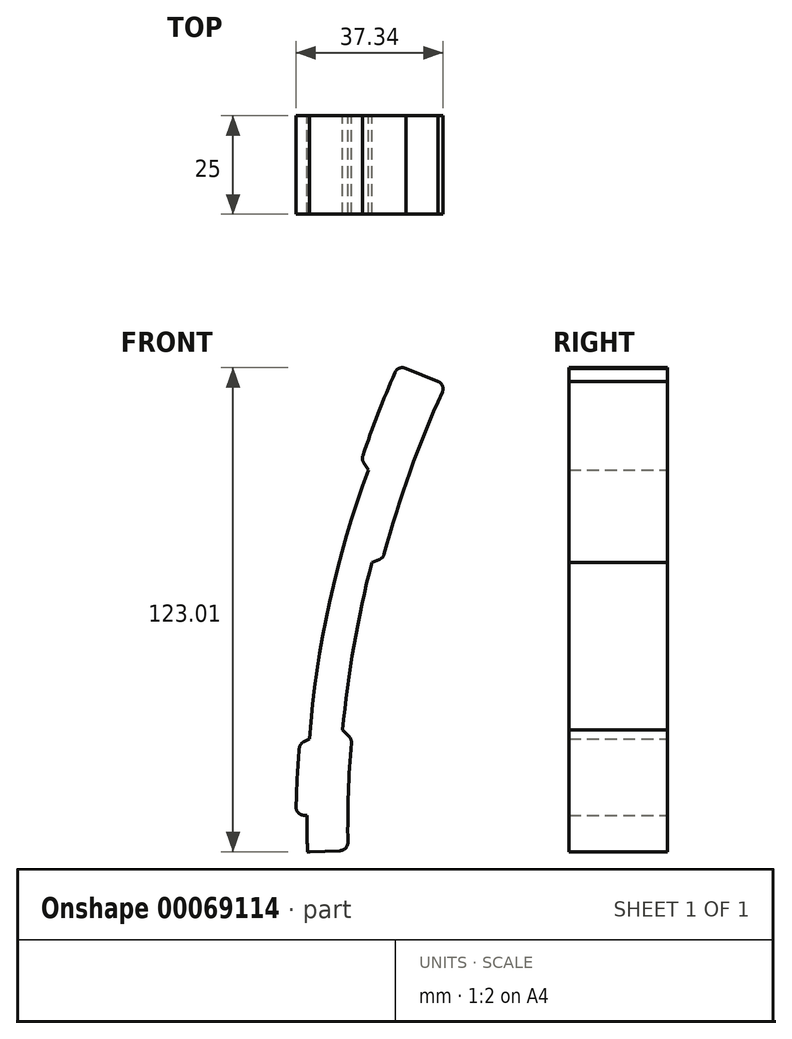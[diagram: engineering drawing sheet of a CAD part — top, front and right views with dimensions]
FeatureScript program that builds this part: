
annotation { "Feature Type Name" : "Feature", "Feature Type Description" : "" }
export const myFeature = defineFeature(function(context is Context, id is Id, definition is map)
    precondition{}
    {
        {
            var Q0;
            Q0=qCreatedBy(makeId("Front.planeOp"),FACE);
            var sketch = newSketch(context, id + "F0", { "sketchPlane" : qUnion([Q0])});
            skArc(sketch, "E0", {"start": v(-249.8, -10) * mm, "mid": v(-249.94, -5.35) * mm, "end": v(-250, -0.7) * mm});
            skArc(sketch, "E1", {"start": v(-250, -10) * mm, "mid": v(-249.6, -10) * mm, "end": v(-249.2, -9.97) * mm});
            skLineSegment(sketch, "E2", {"start": v(-250, -10) * mm, "end": v(-249.2, -9.97) * mm});
            skLineSegment(sketch, "E3", {"start": v(-249.2, -9.97) * mm, "end": v(-241.5, -9.71) * mm});
            skArc(sketch, "E4.trimOffspring", {"start": v(-249.3, 18.65) * mm, "mid": v(-244.24, 53.37) * mm, "end": v(-234.36, 87.04) * mm});
            skArc(sketch, "E5.0", {"start": v(-239.57, -7.69) * mm, "mid": v(-239.42, 5.02) * mm, "end": v(-238.68, 17.71) * mm});
            skArc(sketch, "E6.trimOffspring", {"start": v(-230.32, 65.64) * mm, "mid": v(-223.78, 86.53) * mm, "end": v(-215.57, 106.83) * mm});
            skPoint(sketch, "E7.orphan", {"position": v(-239.02, 13.06) * mm});
            skLineSegment(sketch, "E8", {"start": v(-249.13, 20.78) * mm, "end": v(-249.1, 20.8) * mm});
            skPoint(sketch, "E9.orphan", {"position": v(-248.95, 22.84) * mm});
            skPoint(sketch, "E10.orphan", {"position": v(-250, 1) * mm});
            skArc(sketch, "E11.0", {"start": v(-252.73, 1.35) * mm, "mid": v(-252.42, 8.82) * mm, "end": v(-251.92, 16.27) * mm});
            skArc(sketch, "E12.0", {"start": v(-235.77, 90.65) * mm, "mid": v(-231.9, 101.3) * mm, "end": v(-227.6, 111.8) * mm});
            skArc(sketch, "E13.0", {"start": v(-240.9, 20.93) * mm, "mid": v(-238.03, 42.38) * mm, "end": v(-233.46, 63.54) * mm});
            skLineSegment(sketch, "E14", {"start": v(-233.46, 63.54) * mm, "end": v(-231.53, 64.3) * mm});
            skLineSegment(sketch, "E15", {"start": v(-240.9, 20.93) * mm, "end": v(-239.26, 19.3) * mm});
            skLineSegment(sketch, "E16", {"start": v(-250.81, 17.9) * mm, "end": v(-249.08, 18.76) * mm});
            skPoint(sketch, "E17.visualSharp", {"position": v(-251.83, 17.4) * mm});
            skArc(sketch, "E17.filletArc", {"start": v(-250.81, 17.9) * mm, "mid": v(-251.58, 17.23) * mm, "end": v(-251.92, 16.27) * mm});
            skPoint(sketch, "E18.visualSharp", {"position": v(-252.84, -5.16) * mm});
            skPoint(sketch, "E19.visualSharp", {"position": v(-238.6, 18.64) * mm});
            skArc(sketch, "E19.filletArc", {"start": v(-238.68, 17.71) * mm, "mid": v(-238.8, 18.57) * mm, "end": v(-239.26, 19.3) * mm});
            skPoint(sketch, "E20.visualSharp", {"position": v(-230.58, 64.67) * mm});
            skArc(sketch, "E20.filletArc", {"start": v(-231.53, 64.3) * mm, "mid": v(-230.77, 64.83) * mm, "end": v(-230.32, 65.64) * mm});
            skLineSegment(sketch, "E21", {"start": v(-235.56, 88.94) * mm, "end": v(-234.24, 86.84) * mm});
            skPoint(sketch, "E22.end.orphan", {"position": v(-235.31, 84.43) * mm});
            skPoint(sketch, "E23.visualSharp", {"position": v(-236.07, 89.74) * mm});
            skArc(sketch, "E23.filletArc", {"start": v(-235.77, 90.65) * mm, "mid": v(-235.86, 89.77) * mm, "end": v(-235.56, 88.94) * mm});
            skPoint(sketch, "E24.visualSharp", {"position": v(-226.69, 113.86) * mm});
            skArc(sketch, "E24.filletArc", {"start": v(-224.75, 112.73) * mm, "mid": v(-226.38, 112.9) * mm, "end": v(-227.6, 111.8) * mm});
            skPoint(sketch, "E25.visualSharp", {"position": v(-252.82, -3.11) * mm});
            skLineSegment(sketch, "E26", {"start": v(-250.73, -0.7) * mm, "end": v(-250, -0.7) * mm});
            skArc(sketch, "E27.trimOffspring", {"start": v(-250, 0) * mm, "mid": v(-250, 0) * mm, "end": v(-250, 0) * mm});
            skPoint(sketch, "E28.visualSharp", {"position": v(-252.78, -0.7) * mm});
            skArc(sketch, "E28.filletArc", {"start": v(-252.73, 1.35) * mm, "mid": v(-252.16, -0.1) * mm, "end": v(-250.73, -0.7) * mm});
            skPoint(sketch, "E29.visualSharp", {"position": v(-239.54, -9.65) * mm});
            skArc(sketch, "E29.filletArc", {"start": v(-241.5, -9.71) * mm, "mid": v(-240.13, -9.1) * mm, "end": v(-239.57, -7.69) * mm});
            skPoint(sketch, "E30.visualSharp", {"position": v(-214.67, 108.79) * mm});
            skArc(sketch, "E30.filletArc", {"start": v(-215.57, 106.83) * mm, "mid": v(-215.55, 108.43) * mm, "end": v(-216.7, 109.53) * mm});
            skPoint(sketch, "E31.end.orphan", {"position": v(-223.5, 112) * mm});
            skLineSegment(sketch, "E32", {"start": v(-224.75, 112.73) * mm, "end": v(-216.7, 109.53) * mm});
            skSolve(sketch);
        }
        {
            var Q0;
            Q0 = qSketchRegion(id + "F0", true);
            extrude(context, id + "F1", {"entities" : qUnion([Q0]), "depth" : 25 * mm});
        }
    });
